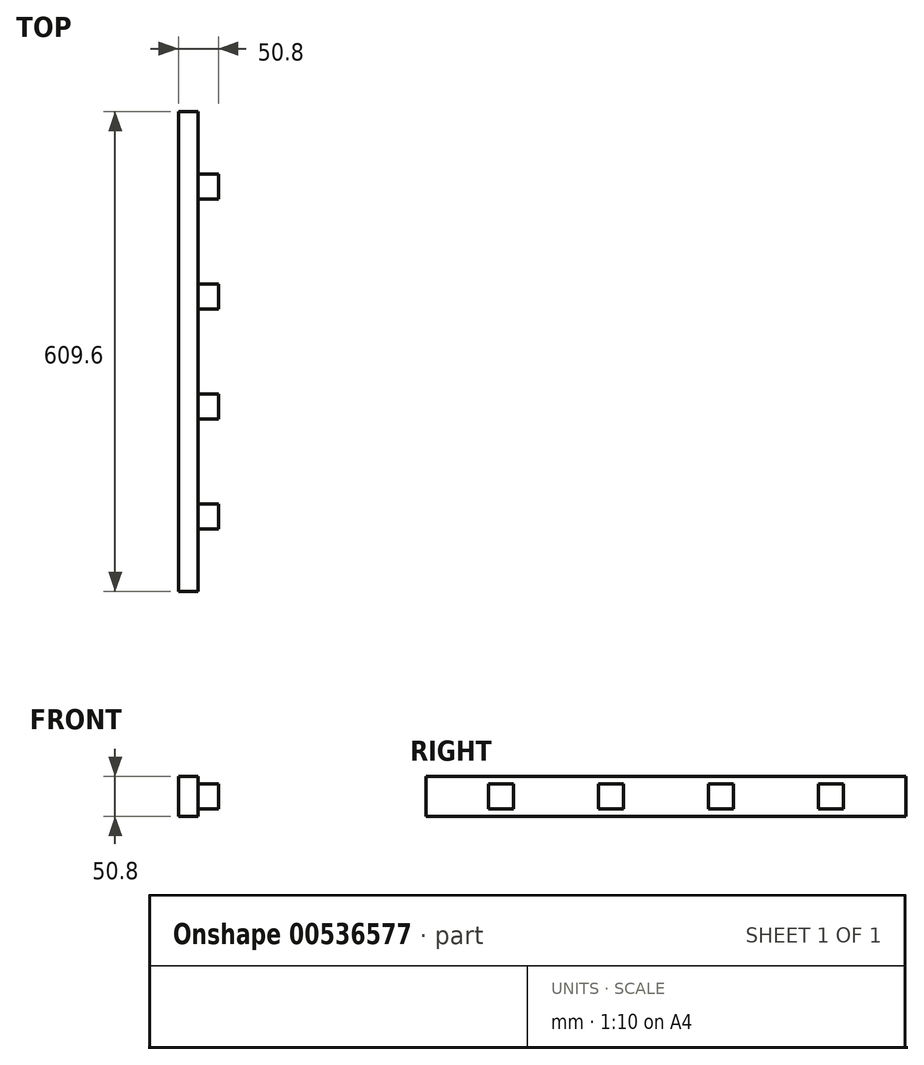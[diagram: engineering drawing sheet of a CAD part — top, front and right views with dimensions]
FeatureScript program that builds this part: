
annotation { "Feature Type Name" : "Feature", "Feature Type Description" : "" }
export const myFeature = defineFeature(function(context is Context, id is Id, definition is map)
    precondition{}
    {
        {
            var Q0;
            Q0=qCreatedBy(makeId("Right.planeOp"),FACE);
            var sketch = newSketch(context, id + "F0", { "sketchPlane" : qUnion([Q0])});
            skLineSegment(sketch, "E0.bottom", {"start": v(-304.8, -65.52) * mm, "end": v(304.8, -65.52) * mm});
            skLineSegment(sketch, "E0.top", {"start": v(-304.8, -116.32) * mm, "end": v(304.8, -116.32) * mm});
            skLineSegment(sketch, "E0.left", {"start": v(-304.8, -65.52) * mm, "end": v(-304.8, -116.32) * mm});
            skLineSegment(sketch, "E0.right", {"start": v(304.8, -65.52) * mm, "end": v(304.8, -116.32) * mm});
            skSolve(sketch);
        }
        {
            var Q0;
            Q0 = qSketchRegion(id + "F0", true);
            extrude(context, id + "F1", {"entities" : qUnion([Q0]), "depth" : 25.4 * mm, "offsetDistance" : 25.4 * mm});
        }
        {
            var Q0;
            Q0=makeQuery(id+"F1.opExtrude","CAP_FACE",FACE,{"disambiguationData":[OSD([sQuery(id+"F0.wireOp",EDGE,"E0.bottom"),sQuery(id+"F0.wireOp",EDGE,"E0.top"),sQuery(id+"F0.wireOp",EDGE,"E0.left"),sQuery(id+"F0.wireOp",EDGE,"E0.right")])],"isStart":false});
            var sketch = newSketch(context, id + "F2", { "sketchPlane" : qUnion([Q0])});
            skLineSegment(sketch, "E1.bottom", {"start": v(-225.42, -75.04) * mm, "end": v(-193.68, -75.04) * mm});
            skLineSegment(sketch, "E1.top", {"start": v(-225.42, -106.8) * mm, "end": v(-193.68, -106.8) * mm});
            skLineSegment(sketch, "E1.left", {"start": v(-225.42, -75.04) * mm, "end": v(-225.42, -106.8) * mm});
            skLineSegment(sketch, "E1.right", {"start": v(-193.68, -75.04) * mm, "end": v(-193.68, -106.8) * mm});
            skLineSegment(sketch, "E2.bottom", {"start": v(-85.73, -75.04) * mm, "end": v(-53.97, -75.04) * mm});
            skLineSegment(sketch, "E2.top", {"start": v(-85.73, -106.8) * mm, "end": v(-53.97, -106.8) * mm});
            skLineSegment(sketch, "E2.left", {"start": v(-85.73, -75.04) * mm, "end": v(-85.73, -106.8) * mm});
            skLineSegment(sketch, "E2.right", {"start": v(-53.98, -75.04) * mm, "end": v(-53.98, -106.8) * mm});
            skLineSegment(sketch, "E3.bottom", {"start": v(53.98, -75.04) * mm, "end": v(85.73, -75.04) * mm});
            skLineSegment(sketch, "E3.top", {"start": v(53.98, -106.8) * mm, "end": v(85.73, -106.8) * mm});
            skLineSegment(sketch, "E3.left", {"start": v(53.98, -75.04) * mm, "end": v(53.98, -106.8) * mm});
            skLineSegment(sketch, "E3.right", {"start": v(85.73, -75.04) * mm, "end": v(85.73, -106.8) * mm});
            skLineSegment(sketch, "E4.bottom", {"start": v(193.67, -75.04) * mm, "end": v(225.42, -75.04) * mm});
            skLineSegment(sketch, "E4.top", {"start": v(193.67, -106.8) * mm, "end": v(225.42, -106.8) * mm});
            skLineSegment(sketch, "E4.left", {"start": v(193.67, -75.04) * mm, "end": v(193.67, -106.8) * mm});
            skLineSegment(sketch, "E4.right", {"start": v(225.42, -75.04) * mm, "end": v(225.42, -106.8) * mm});
            skSolve(sketch);
        }
        {
            var Q0;
            Q0 = qSketchRegion(id + "F2", true);
            extrude(context, id + "F3", {"entities" : qUnion([Q0]), "operationType" : NewBodyOperationType.ADD, "depth" : 25.4 * mm, "offsetDistance" : 25.4 * mm});
        }
    });
